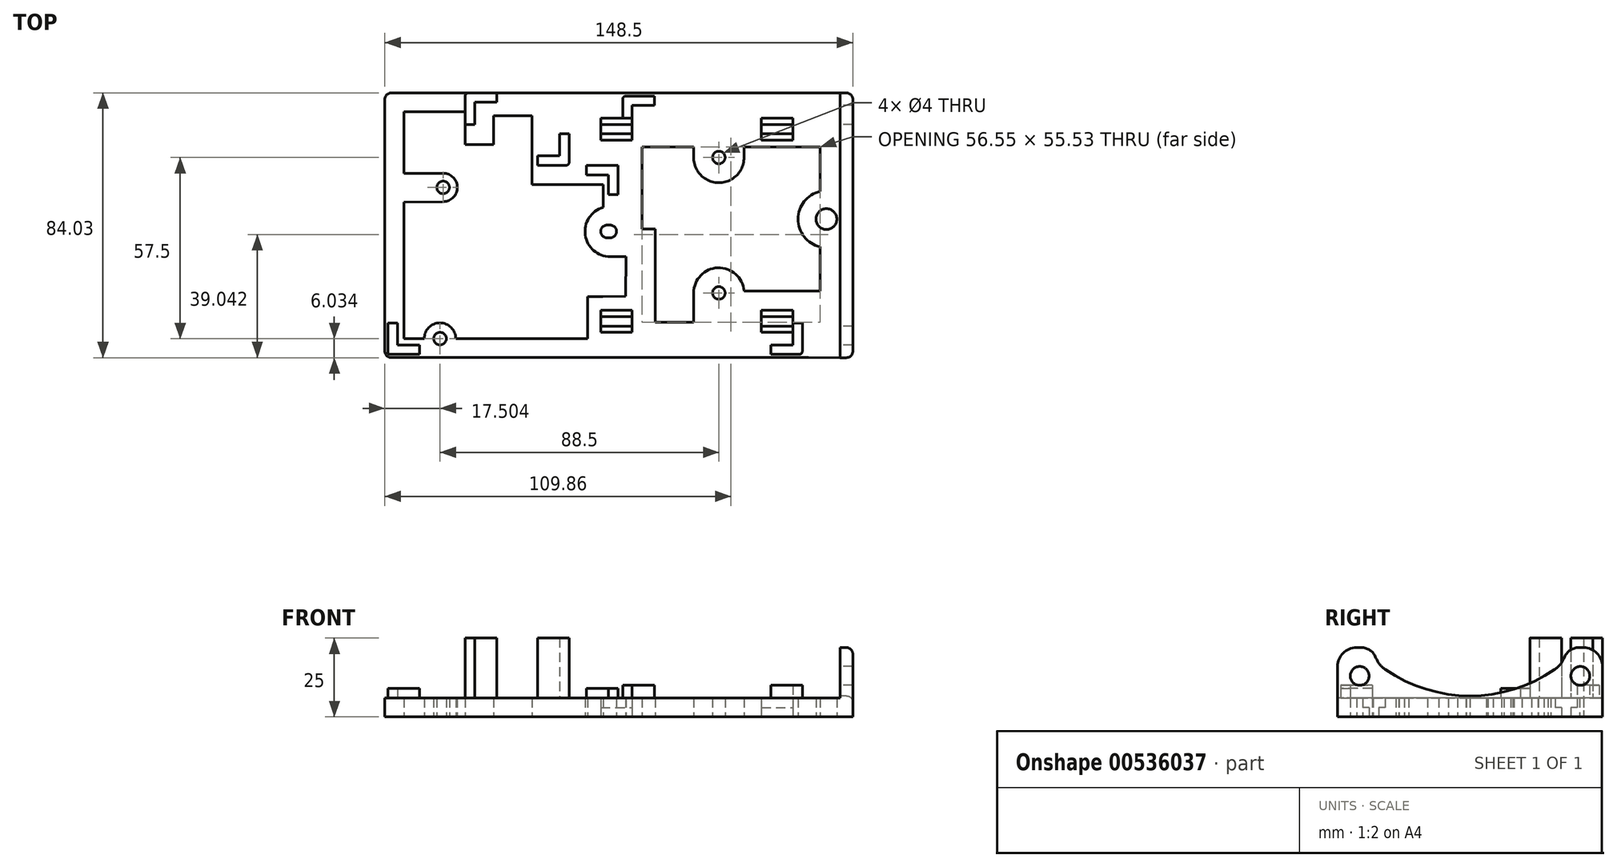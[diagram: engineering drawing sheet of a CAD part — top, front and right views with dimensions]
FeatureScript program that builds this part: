
annotation { "Feature Type Name" : "Feature", "Feature Type Description" : "" }
export const myFeature = defineFeature(function(context is Context, id is Id, definition is map)
    precondition{}
    {
        {
            var Q0;
            Q0=qCreatedBy(makeId("Top.planeOp"),FACE);
            var sketch = newSketch(context, id + "F0", { "sketchPlane" : qUnion([Q0]), "disableImprinting" : false});
            skLineSegment(sketch, "E0.bottom", {"start": v(-72.26, -23.08) * mm, "end": v(47.74, -23.08) * mm});
            skLineSegment(sketch, "E0.top", {"start": v(-72.26, 60.92) * mm, "end": v(47.74, 60.92) * mm});
            skLineSegment(sketch, "E1.bottom", {"start": v(42.74, 56.92) * mm, "end": v(-8.26, 56.92) * mm});
            skLineSegment(sketch, "E1.top", {"start": v(42.74, -19.08) * mm, "end": v(-8.26, -19.08) * mm});
            skLineSegment(sketch, "E1.right", {"start": v(-8.26, 56.92) * mm, "end": v(-8.26, -19.08) * mm});
            skLineSegment(sketch, "E2", {"start": v(-1.26, 56.92) * mm, "end": v(-1.26, 59.92) * mm});
            skLineSegment(sketch, "E3", {"start": v(-1.26, 59.92) * mm, "end": v(-11.26, 59.92) * mm});
            skLineSegment(sketch, "E4", {"start": v(-8.26, 49.92) * mm, "end": v(-8.26, 56.92) * mm});
            skLineSegment(sketch, "E5", {"start": v(35.74, -19.08) * mm, "end": v(35.74, -22.08) * mm});
            skLineSegment(sketch, "E6", {"start": v(35.74, -22.08) * mm, "end": v(45.74, -22.08) * mm});
            skLineSegment(sketch, "E7", {"start": v(45.74, -22.08) * mm, "end": v(45.74, -12.08) * mm});
            skLineSegment(sketch, "E8", {"start": v(45.74, -12.08) * mm, "end": v(42.74, -12.08) * mm});
            skLineSegment(sketch, "E9", {"start": v(42.74, -12.08) * mm, "end": v(42.74, -19.08) * mm});
            skCircle(sketch, "E10", {"center": v(19.24, 40.42) * mm, "radius": 2 * mm});
            skCircle(sketch, "E11.MirrorC", {"center": v(19.24, -2.58) * mm, "radius": 2 * mm});
            skLineSegment(sketch, "E12", {"start": v(47.74, 60.92) * mm, "end": v(57.74, 60.92) * mm});
            skLineSegment(sketch, "E13", {"start": v(57.74, 60.92) * mm, "end": v(57.74, -23.11) * mm});
            skLineSegment(sketch, "E14", {"start": v(57.74, -23.11) * mm, "end": v(47.74, -23.08) * mm});
            skLineSegment(sketch, "E15.bottom", {"start": v(-72.26, -23.08) * mm, "end": v(-86.76, -23.08) * mm});
            skLineSegment(sketch, "E15.left", {"start": v(-72.26, -23.08) * mm, "end": v(-72.26, -23.08) * mm});
            skLineSegment(sketch, "E15.right", {"start": v(-86.76, -23.08) * mm, "end": v(-86.76, -23.08) * mm});
            skLineSegment(sketch, "E16.bottom", {"start": v(-86.76, -23.08) * mm, "end": v(-72.26, -23.08) * mm});
            skLineSegment(sketch, "E16.top", {"start": v(-86.76, 60.92) * mm, "end": v(-72.26, 60.92) * mm});
            skLineSegment(sketch, "E16.left", {"start": v(-86.76, -23.08) * mm, "end": v(-86.76, 60.92) * mm});
            skLineSegment(sketch, "E17", {"start": v(-85.76, -12.08) * mm, "end": v(-85.76, -22.08) * mm});
            skLineSegment(sketch, "E18", {"start": v(-85.76, -22.08) * mm, "end": v(-75.76, -22.08) * mm});
            skLineSegment(sketch, "E19", {"start": v(-75.76, -22.08) * mm, "end": v(-75.76, -19.08) * mm});
            skLineSegment(sketch, "E20", {"start": v(-75.76, -19.08) * mm, "end": v(-82.76, -19.08) * mm});
            skLineSegment(sketch, "E21", {"start": v(-22.76, 34.92) * mm, "end": v(-22.76, 37.92) * mm});
            skLineSegment(sketch, "E22", {"start": v(-22.76, 37.92) * mm, "end": v(-12.76, 37.92) * mm});
            skLineSegment(sketch, "E23", {"start": v(-12.76, 37.92) * mm, "end": v(-12.76, 28.7) * mm});
            skLineSegment(sketch, "E24", {"start": v(-12.76, 28.7) * mm, "end": v(-15.76, 28.7) * mm});
            skLineSegment(sketch, "E25", {"start": v(-15.76, 28.7) * mm, "end": v(-15.76, 34.92) * mm});
            skCircle(sketch, "E26", {"center": v(-69.26, -17.08) * mm, "radius": 2 * mm});
            skArc(sketch, "E27", {"start": v(-15.24, 14.92) * mm, "mid": v(-13.23, 16.93) * mm, "end": v(-15.24, 18.94) * mm});
            skLineSegment(sketch, "E28", {"start": v(-22.76, 34.92) * mm, "end": v(-15.76, 34.92) * mm});
            skLineSegment(sketch, "E29", {"start": v(-82.76, -12.08) * mm, "end": v(-82.76, -19.08) * mm});
            skLineSegment(sketch, "E30", {"start": v(-51.26, 57.92) * mm, "end": v(-51.26, 60.92) * mm});
            skLineSegment(sketch, "E31", {"start": v(-51.26, 60.92) * mm, "end": v(-61.26, 60.92) * mm});
            skLineSegment(sketch, "E32", {"start": v(-61.26, 60.92) * mm, "end": v(-61.26, 50.92) * mm});
            skLineSegment(sketch, "E33", {"start": v(-61.26, 50.92) * mm, "end": v(-58.26, 50.92) * mm});
            skLineSegment(sketch, "E34", {"start": v(-38.26, 40.92) * mm, "end": v(-38.26, 37.92) * mm});
            skLineSegment(sketch, "E35", {"start": v(-38.26, 37.92) * mm, "end": v(-28.26, 37.92) * mm});
            skLineSegment(sketch, "E36", {"start": v(-28.26, 37.92) * mm, "end": v(-28.26, 47.92) * mm});
            skLineSegment(sketch, "E37", {"start": v(-28.26, 47.92) * mm, "end": v(-31.26, 47.92) * mm});
            skLineSegment(sketch, "E38", {"start": v(-31.26, 47.92) * mm, "end": v(-31.26, 40.92) * mm});
            skLineSegment(sketch, "E39", {"start": v(-38.26, 40.92) * mm, "end": v(-31.26, 40.92) * mm});
            skLineSegment(sketch, "E40", {"start": v(-58.26, 57.92) * mm, "end": v(-51.26, 57.92) * mm});
            skLineSegment(sketch, "E41", {"start": v(-58.26, 57.92) * mm, "end": v(-58.26, 50.92) * mm});
            skLineSegment(sketch, "E42.bottom", {"start": v(32.74, -8.08) * mm, "end": v(42.74, -8.08) * mm});
            skLineSegment(sketch, "E42.top", {"start": v(32.74, -15.08) * mm, "end": v(42.74, -15.08) * mm});
            skLineSegment(sketch, "E42.left", {"start": v(32.74, -8.08) * mm, "end": v(32.74, -15.08) * mm});
            skLineSegment(sketch, "E42.right", {"start": v(42.74, -8.08) * mm, "end": v(42.74, -15.08) * mm});
            skLineSegment(sketch, "E43.bottom", {"start": v(-18.26, -8.08) * mm, "end": v(-8.26, -8.08) * mm});
            skLineSegment(sketch, "E43.top", {"start": v(-18.26, -15.08) * mm, "end": v(-8.26, -15.08) * mm});
            skLineSegment(sketch, "E43.left", {"start": v(-18.26, -8.08) * mm, "end": v(-18.26, -15.08) * mm});
            skLineSegment(sketch, "E43.right", {"start": v(-8.26, -8.08) * mm, "end": v(-8.26, -15.08) * mm});
            skLineSegment(sketch, "E44", {"start": v(-18.26, -13.08) * mm, "end": v(-8.26, -13.08) * mm});
            skLineSegment(sketch, "E45", {"start": v(-18.26, -10.08) * mm, "end": v(-8.26, -10.08) * mm});
            skLineSegment(sketch, "E46", {"start": v(32.74, -10.08) * mm, "end": v(42.74, -10.08) * mm});
            skLineSegment(sketch, "E47", {"start": v(32.74, -13.08) * mm, "end": v(42.74, -13.08) * mm});
            skLineSegment(sketch, "E48.bottom", {"start": v(42.74, 52.92) * mm, "end": v(32.74, 52.92) * mm});
            skLineSegment(sketch, "E48.top", {"start": v(42.74, 45.92) * mm, "end": v(32.74, 45.92) * mm});
            skLineSegment(sketch, "E48.left", {"start": v(42.74, 52.92) * mm, "end": v(42.74, 45.92) * mm});
            skLineSegment(sketch, "E48.right", {"start": v(32.74, 52.92) * mm, "end": v(32.74, 45.92) * mm});
            skLineSegment(sketch, "E49", {"start": v(32.74, 50.92) * mm, "end": v(42.74, 50.92) * mm});
            skLineSegment(sketch, "E50", {"start": v(32.74, 47.92) * mm, "end": v(42.74, 47.92) * mm});
            skLineSegment(sketch, "E51.bottom", {"start": v(-18.26, 52.92) * mm, "end": v(-8.26, 52.92) * mm});
            skLineSegment(sketch, "E51.top", {"start": v(-18.26, 45.92) * mm, "end": v(-8.26, 45.92) * mm});
            skLineSegment(sketch, "E51.left", {"start": v(-18.26, 52.92) * mm, "end": v(-18.26, 45.92) * mm});
            skLineSegment(sketch, "E51.right", {"start": v(-8.26, 52.92) * mm, "end": v(-8.26, 45.92) * mm});
            skLineSegment(sketch, "E52", {"start": v(-18.26, 47.92) * mm, "end": v(-8.26, 47.92) * mm});
            skLineSegment(sketch, "E53", {"start": v(-11.26, 59.92) * mm, "end": v(-11.26, 52.92) * mm});
            skLineSegment(sketch, "E54", {"start": v(-11.26, 52.92) * mm, "end": v(-8.26, 52.92) * mm});
            skLineSegment(sketch, "E55", {"start": v(-18.26, 50.92) * mm, "end": v(-8.26, 50.92) * mm});
            skPoint(sketch, "E56.endSnap0", {"position": v(-15.76, 31.81) * mm});
            skLineSegment(sketch, "E57", {"start": v(-17.51, 31.81) * mm, "end": v(-40.11, 31.81) * mm});
            skLineSegment(sketch, "E58", {"start": v(-40.11, 31.81) * mm, "end": v(-40.11, 53.65) * mm});
            skLineSegment(sketch, "E59", {"start": v(-40.11, 53.65) * mm, "end": v(-52.22, 53.65) * mm});
            skLineSegment(sketch, "E60", {"start": v(-52.22, 53.65) * mm, "end": v(-52.22, 44.5) * mm});
            skLineSegment(sketch, "E61", {"start": v(-52.22, 44.5) * mm, "end": v(-61.24, 44.5) * mm});
            skLineSegment(sketch, "E62", {"start": v(-61.24, 44.5) * mm, "end": v(-61.24, 54.92) * mm});
            skLineSegment(sketch, "E63", {"start": v(-61.24, 54.92) * mm, "end": v(-80.76, 54.92) * mm});
            skLineSegment(sketch, "E64", {"start": v(-85.76, -12.08) * mm, "end": v(-82.76, -12.08) * mm});
            skLineSegment(sketch, "E65", {"start": v(-22.37, -17.08) * mm, "end": v(-22.37, -3.68) * mm});
            skLineSegment(sketch, "E66", {"start": v(-22.37, -3.68) * mm, "end": v(-17.57, -3.68) * mm});
            skLineSegment(sketch, "E67", {"start": v(-10.28, 8.95) * mm, "end": v(-10.3, -3.62) * mm});
            skLineSegment(sketch, "E68", {"start": v(-10.3, -3.62) * mm, "end": v(-17.57, -3.68) * mm});
            skLineSegment(sketch, "E69", {"start": v(-64.26, -17.08) * mm, "end": v(-22.37, -17.08) * mm});
            skLineSegment(sketch, "E70", {"start": v(-5.17, 43.7) * mm, "end": v(-5.17, 17.78) * mm});
            skLineSegment(sketch, "E71", {"start": v(-5.17, 17.78) * mm, "end": v(-0.94, 17.78) * mm});
            skLineSegment(sketch, "E72", {"start": v(-0.94, 17.78) * mm, "end": v(-0.94, -5.91) * mm});
            skLineSegment(sketch, "E73", {"start": v(-0.94, -5.91) * mm, "end": v(-0.94, -11.83) * mm});
            skLineSegment(sketch, "E74", {"start": v(-0.94, -11.83) * mm, "end": v(11.24, -11.83) * mm});
            skLineSegment(sketch, "E75", {"start": v(11.24, -11.83) * mm, "end": v(11.24, -2.58) * mm});
            skLineSegment(sketch, "E76", {"start": v(27.22, -1.96) * mm, "end": v(51.37, -1.96) * mm});
            skLineSegment(sketch, "E77", {"start": v(51.37, 43.7) * mm, "end": v(51.37, 29.64) * mm});
            skArc(sketch, "E78", {"start": v(11.24, -2.58) * mm, "mid": v(18.94, 5.42) * mm, "end": v(27.22, -1.96) * mm});
            skLineSegment(sketch, "E79", {"start": v(11.25, 40.65) * mm, "end": v(11.25, 43.7) * mm});
            skLineSegment(sketch, "E80", {"start": v(27.24, 40.53) * mm, "end": v(27.24, 43.7) * mm});
            skArc(sketch, "E81", {"start": v(27.24, 40.53) * mm, "mid": v(19.18, 32.42) * mm, "end": v(11.25, 40.65) * mm});
            skLineSegment(sketch, "E82", {"start": v(-5.17, 43.7) * mm, "end": v(11.25, 43.7) * mm});
            skLineSegment(sketch, "E83", {"start": v(27.24, 43.7) * mm, "end": v(51.37, 43.7) * mm});
            skArc(sketch, "E84", {"start": v(-15.24, 8.95) * mm, "mid": v(-23.14, 15.78) * mm, "end": v(-17.51, 24.6) * mm});
            skLineSegment(sketch, "E85", {"start": v(-17.51, 31.81) * mm, "end": v(-17.51, 24.6) * mm});
            skLineSegment(sketch, "E86", {"start": v(-80.76, 54.92) * mm, "end": v(-80.76, 39.92) * mm});
            skLineSegment(sketch, "E87", {"start": v(-80.76, 25.92) * mm, "end": v(-80.76, -17.08) * mm});
            skArc(sketch, "E88", {"start": v(-64.26, -17.08) * mm, "mid": v(-69.26, -12.08) * mm, "end": v(-74.26, -17.08) * mm});
            skLineSegment(sketch, "E89", {"start": v(-80.76, -17.08) * mm, "end": v(-74.26, -17.08) * mm});
            skCircle(sketch, "E90", {"center": v(-68.26, 30.92) * mm, "radius": 2 * mm});
            skLineSegment(sketch, "E91", {"start": v(-68.26, 35.42) * mm, "end": v(-80.76, 35.42) * mm});
            skLineSegment(sketch, "E92", {"start": v(-68.2, 26.42) * mm, "end": v(-80.76, 26.24) * mm});
            skArc(sketch, "E93", {"start": v(-68.2, 26.42) * mm, "mid": v(-63.76, 30.95) * mm, "end": v(-68.26, 35.42) * mm});
            skLineSegment(sketch, "E94", {"start": v(-80.76, 39.92) * mm, "end": v(-80.76, 35.42) * mm});
            skLineSegment(sketch, "E95", {"start": v(-80.76, 25.92) * mm, "end": v(-80.76, 26.24) * mm});
            skLineSegment(sketch, "E96.trimOffspring", {"start": v(51.37, 12.1) * mm, "end": v(51.37, -1.96) * mm});
            skCircle(sketch, "E97", {"center": v(53.37, 20.87) * mm, "radius": 3.3 * mm});
            skArc(sketch, "E98", {"start": v(51.37, 29.64) * mm, "mid": v(44.37, 20.87) * mm, "end": v(51.37, 12.1) * mm});
            skArc(sketch, "E99", {"start": v(-16.24, 18.94) * mm, "mid": v(-18.26, 16.94) * mm, "end": v(-16.26, 14.92) * mm});
            skLineSegment(sketch, "E100", {"start": v(-16.24, 18.94) * mm, "end": v(-15.24, 18.94) * mm});
            skLineSegment(sketch, "E101", {"start": v(-16.26, 14.92) * mm, "end": v(-15.24, 14.92) * mm});
            skLineSegment(sketch, "E102", {"start": v(-15.24, 8.95) * mm, "end": v(-10.28, 8.95) * mm});
            skSolve(sketch);
        }
        {
            var Q0;
            Q0=makeQuery(id+"F0.imprint","IMPRINT",FACE,{"disambiguationData":[TD([[makeQuery(id+"F0.imprint","IMPRINT",EDGE,{"derivedFrom":sQuery(id+"F0.wireOp",EDGE,"E0.bottom")}),1.0]])]});
            var Q1;
            {var subQ7=sQuery(id+"F0.wireOp",EDGE,"E1.left");Q1=makeQuery(id+"F0.imprint","IMPRINT",FACE,{"disambiguationData":[TD([[makeQuery(id+"F0.imprint","IMPRINT",EDGE,{"derivedFrom":subQ7}),-1.0]])]});}
            extrude(context, id + "F1", {"entities" : qUnion([Q0, Q1]), "depth" : 6 * mm, "offsetDistance" : 25 * mm});
        }
        {
            var Q0;
            {var subQ3=sQuery(id+"F0.wireOp",EDGE,"E2");Q0=makeQuery(id+"F0.imprint","IMPRINT",FACE,{"disambiguationData":[TD([[makeQuery(id+"F0.imprint","IMPRINT",EDGE,{"derivedFrom":subQ3}),1.0]])]});}
            var Q1;
            {var subQ0=sQuery(id+"F0.wireOp",EDGE,"E5");Q1=makeQuery(id+"F0.imprint","IMPRINT",FACE,{"disambiguationData":[TD([[makeQuery(id+"F0.imprint","IMPRINT",EDGE,{"derivedFrom":subQ0}),1.0]])]});}
            extrude(context, id + "F2", {"entities" : qUnion([Q0, Q1]), "operationType" : NewBodyOperationType.ADD, "depth" : 10 * mm, "offsetDistance" : 25 * mm});
        }
        {
            var Q0;
            Q0=makeQuery(id+"F1.opExtrude","SWEPT_FACE",FACE,{"disambiguationData":[OSD([sQuery(id+"F0.wireOp",EDGE,"E13")])]});
            var sketch = newSketch(context, id + "F3", { "sketchPlane" : qUnion([Q0])});
            skLineSegment(sketch, "E103", {"start": v(-23.11, 0) * mm, "end": v(-23.11, 22) * mm});
            skLineSegment(sketch, "E104", {"start": v(-23.11, 22) * mm, "end": v(-3.11, 22) * mm});
            skLineSegment(sketch, "E105", {"start": v(-3.11, 22) * mm, "end": v(-3.11, 6) * mm});
            skLineSegment(sketch, "E106", {"start": v(-3.11, 6) * mm, "end": v(40.92, 6) * mm});
            skLineSegment(sketch, "E107", {"start": v(40.92, 6) * mm, "end": v(40.92, 22) * mm});
            skLineSegment(sketch, "E108", {"start": v(40.92, 22) * mm, "end": v(60.92, 22) * mm});
            skLineSegment(sketch, "E109", {"start": v(60.92, 22) * mm, "end": v(60.92, 0) * mm});
            skLineSegment(sketch, "E110", {"start": v(60.92, 0) * mm, "end": v(-23.11, 0) * mm});
            skCircle(sketch, "E111", {"center": v(-3.11, 22) * mm, "radius": 8.5 * mm});
            skCircle(sketch, "E112", {"center": v(40.92, 22) * mm, "radius": 8.5 * mm});
            skCircle(sketch, "E113", {"center": v(-16.11, 13) * mm, "radius": 3 * mm});
            skCircle(sketch, "E114", {"center": v(53.92, 13) * mm, "radius": 3 * mm});
            skLineSegment(sketch, "E115", {"start": v(18.9, 57) * mm, "end": v(18.9, 13.5) * mm});
            skArc(sketch, "E116", {"start": v(45.73, 15) * mm, "mid": v(18.9, 6.67) * mm, "end": v(-7.92, 15) * mm});
            skSolve(sketch);
        }
        {
            var Q0;
            {var subQ0=sQuery(id+"F3.wireOp",EDGE,"E104");var subQ1=sQuery(id+"F3.wireOp",EDGE,"E103");var subQ2=makeQuery(id+"F3.imprint","INTERSECT",VERTEX,{"derivedFrom":[subQ1,subQ0]});Q0=makeQuery(id+"F3.imprint","IMPRINT",FACE,{"disambiguationData":[TD([[makeQuery(id+"F3.imprint","IMPRINT",EDGE,{"disambiguationData":[TD([[subQ2,1.0]])],"derivedFrom":subQ1}),-1.0]])]});}
            var Q1;
            {var subQ6=sQuery(id+"F3.wireOp",EDGE,"E106");Q1=makeQuery(id+"F3.imprint","IMPRINT",FACE,{"disambiguationData":[TD([[makeQuery(id+"F3.imprint","IMPRINT",EDGE,{"derivedFrom":subQ6}),1.0]])]});}
            var Q2;
            {var subQ0=sQuery(id+"F3.wireOp",EDGE,"E106");Q2=makeQuery(id+"F3.imprint","IMPRINT",FACE,{"disambiguationData":[TD([[makeQuery(id+"F3.imprint","IMPRINT",EDGE,{"derivedFrom":subQ0}),-1.0]])]});}
            var Q3;
            {var subQ3=sQuery(id+"F3.wireOp",EDGE,"E108");var subQ7=sQuery(id+"F3.wireOp",EDGE,"E109");var subQ9=makeQuery(id+"F3.imprint","INTERSECT",VERTEX,{"derivedFrom":[subQ3,subQ7]});Q3=makeQuery(id+"F3.imprint","IMPRINT",FACE,{"disambiguationData":[TD([[makeQuery(id+"F3.imprint","IMPRINT",EDGE,{"disambiguationData":[TD([[subQ9,1.0]])],"derivedFrom":subQ3}),-1.0]])]});}
            extrude(context, id + "F4", {"entities" : qUnion([Q0, Q1, Q2, Q3]), "operationType" : NewBodyOperationType.ADD, "depth" : 4 * mm, "offsetDistance" : 25 * mm});
        }
        {
            var Q0;
            Q0=makeQuery(id+"F4.opExtrude","SWEPT_EDGE",EDGE,{"disambiguationData":[OSD([sQuery(id+"F3.wireOp",EDGE,"E104"),sQuery(id+"F3.wireOp",EDGE,"E111")])]});
            fillet(context, id + "F5", {"entities" : qUnion([Q0]), "radius" : 5 * mm, "tangentPropagation" : true, "allowEdgeOverflow" : false});
        }
        {
            var Q0;
            Q0=makeQuery(id+"F4.opExtrude","SWEPT_EDGE",EDGE,{"disambiguationData":[OSD([sQuery(id+"F3.wireOp",EDGE,"E108"),sQuery(id+"F3.wireOp",EDGE,"E112")])]});
            fillet(context, id + "F6", {"entities" : qUnion([Q0]), "radius" : 5 * mm, "tangentPropagation" : true, "allowEdgeOverflow" : false});
        }
        {
            var Q0;
            Q0=makeQuery(id+"F4.opExtrude","SWEPT_EDGE",EDGE,{"disambiguationData":[OSD([sQuery(id+"F3.wireOp",EDGE,"E108"),sQuery(id+"F3.wireOp",EDGE,"E109")])]});
            fillet(context, id + "F7", {"entities" : qUnion([Q0]), "radius" : 6 * mm, "tangentPropagation" : true, "allowEdgeOverflow" : false});
        }
        {
            var Q0;
            Q0=makeQuery(id+"F4.opExtrude","SWEPT_EDGE",EDGE,{"disambiguationData":[OSD([sQuery(id+"F3.wireOp",EDGE,"E103"),sQuery(id+"F3.wireOp",EDGE,"E104")])]});
            fillet(context, id + "F8", {"entities" : qUnion([Q0]), "radius" : 6 * mm, "tangentPropagation" : true, "allowEdgeOverflow" : false});
        }
        {
            var Q0;
            {var subQ4=sQuery(id+"F0.wireOp",EDGE,"E30");Q0=makeQuery(id+"F0.imprint","IMPRINT",FACE,{"disambiguationData":[TD([[makeQuery(id+"F0.imprint","IMPRINT",EDGE,{"derivedFrom":subQ4}),1.0]])]});}
            var Q1;
            Q1=makeQuery(id+"F0.imprint","IMPRINT",FACE,{"disambiguationData":[TD([[makeQuery(id+"F0.imprint","IMPRINT",EDGE,{"derivedFrom":sQuery(id+"F0.wireOp",EDGE,"E34")}),1.0]])]});
            extrude(context, id + "F9", {"entities" : qUnion([Q0, Q1]), "operationType" : NewBodyOperationType.ADD, "depth" : 25 * mm, "offsetDistance" : 25 * mm});
        }
        {
            var Q0;
            {var subQ3=sQuery(id+"F0.wireOp",EDGE,"E55");Q0=makeQuery(id+"F0.imprint","IMPRINT",FACE,{"disambiguationData":[TD([[makeQuery(id+"F0.imprint","IMPRINT",EDGE,{"derivedFrom":subQ3}),1.0]])]});}
            var Q1;
            {var subQ0=sQuery(id+"F0.wireOp",EDGE,"E51.top");Q1=makeQuery(id+"F0.imprint","IMPRINT",FACE,{"disambiguationData":[TD([[makeQuery(id+"F0.imprint","IMPRINT",EDGE,{"derivedFrom":subQ0}),1.0]])]});}
            var Q2;
            {var subQ0=sQuery(id+"F0.wireOp",EDGE,"E48.bottom");Q2=makeQuery(id+"F0.imprint","IMPRINT",FACE,{"disambiguationData":[TD([[makeQuery(id+"F0.imprint","IMPRINT",EDGE,{"derivedFrom":subQ0}),1.0]])]});}
            var Q3;
            {var subQ0=sQuery(id+"F0.wireOp",EDGE,"E48.top");Q3=makeQuery(id+"F0.imprint","IMPRINT",FACE,{"disambiguationData":[TD([[makeQuery(id+"F0.imprint","IMPRINT",EDGE,{"derivedFrom":subQ0}),-1.0]])]});}
            var Q4;
            {var subQ0=sQuery(id+"F0.wireOp",EDGE,"E42.bottom");Q4=makeQuery(id+"F0.imprint","IMPRINT",FACE,{"disambiguationData":[TD([[makeQuery(id+"F0.imprint","IMPRINT",EDGE,{"derivedFrom":subQ0}),-1.0]])]});}
            var Q5;
            {var subQ0=sQuery(id+"F0.wireOp",EDGE,"E42.top");Q5=makeQuery(id+"F0.imprint","IMPRINT",FACE,{"disambiguationData":[TD([[makeQuery(id+"F0.imprint","IMPRINT",EDGE,{"derivedFrom":subQ0}),1.0]])]});}
            var Q6;
            {var subQ0=sQuery(id+"F0.wireOp",EDGE,"E43.top");Q6=makeQuery(id+"F0.imprint","IMPRINT",FACE,{"disambiguationData":[TD([[makeQuery(id+"F0.imprint","IMPRINT",EDGE,{"derivedFrom":subQ0}),1.0]])]});}
            var Q7;
            {var subQ0=sQuery(id+"F0.wireOp",EDGE,"E43.bottom");Q7=makeQuery(id+"F0.imprint","IMPRINT",FACE,{"disambiguationData":[TD([[makeQuery(id+"F0.imprint","IMPRINT",EDGE,{"derivedFrom":subQ0}),-1.0]])]});}
            extrude(context, id + "F10", {"entities" : qUnion([Q0, Q1, Q2, Q3, Q4, Q5, Q6, Q7]), "operationType" : NewBodyOperationType.ADD, "depth" : 3 * mm, "offsetDistance" : 25 * mm});
        }
        {
            var Q0;
            Q0=makeQuery(id+"Ffwyr1q8zjNAo8w_0.opExtrude","SWEPT_EDGE",EDGE,{"disambiguationData":[OSD([sQuery(id+"F0.wireOp",EDGE,"E17"),sQuery(id+"F0.wireOp",EDGE,"E18")])]});
            var Q1;
            Q1=makeQuery(id+"F1.opExtrude","SWEPT_EDGE",EDGE,{"disambiguationData":[OSD([sQuery(id+"F0.wireOp",EDGE,"E15.bottom"),sQuery(id+"F0.wireOp",EDGE,"E16.left")])]});
            fillet(context, id + "F11", {"entities" : qUnion([Q0, Q1]), "radius" : 2 * mm, "tangentPropagation" : true, "allowEdgeOverflow" : false});
        }
        {
            var Q0;
            Q0=makeQuery(id+"F2.opExtrude","SWEPT_EDGE",EDGE,{"disambiguationData":[OSD([sQuery(id+"F0.wireOp",EDGE,"E3"),sQuery(id+"F0.wireOp",EDGE,"E53")])]});
            var Q1;
            Q1=makeQuery(id+"F9.opExtrude","SWEPT_EDGE",EDGE,{"disambiguationData":[OSD([sQuery(id+"F0.wireOp",EDGE,"E0.top"),sQuery(id+"F0.wireOp",EDGE,"E32")])]});
            var Q2;
            Q2=makeQuery(id+"F2.opExtrude","SWEPT_EDGE",EDGE,{"disambiguationData":[OSD([sQuery(id+"F0.wireOp",EDGE,"E6"),sQuery(id+"F0.wireOp",EDGE,"E7")])]});
            var Q3;
            Q3=makeQuery(id+"F9.opExtrude","SWEPT_EDGE",EDGE,{"disambiguationData":[OSD([sQuery(id+"F0.wireOp",EDGE,"E35"),sQuery(id+"F0.wireOp",EDGE,"E36")])]});
            var Q4;
            Q4=makeQuery(id+"FGamisbfVxoSGgb_0.opExtrude","SWEPT_EDGE",EDGE,{"disambiguationData":[OSD([sQuery(id+"F0.wireOp",EDGE,"E22"),sQuery(id+"F0.wireOp",EDGE,"E23")])]});
            fillet(context, id + "F12", {"entities" : qUnion([Q0, Q1, Q2, Q3, Q4]), "radius" : 1 * mm, "tangentPropagation" : true, "allowEdgeOverflow" : false});
        }
        {
            var Q0;
            Q0=makeQuery(id+"F4.opExtrude","CAP_EDGE",EDGE,{"disambiguationData":[OSD([sQuery(id+"F3.wireOp",EDGE,"E116")])],"isStart":false});
            var Q1;
            Q1=makeQuery(id+"F4.opExtrude","CAP_EDGE",EDGE,{"disambiguationData":[OSD([sQuery(id+"F3.wireOp",EDGE,"E112")])],"isStart":false});
            var Q2;
            {var subQ0=sQuery(id+"F3.wireOp",EDGE,"E109");var subQ1=sQuery(id+"F3.wireOp",EDGE,"E108");Q2=makeQuery(id+"F7.opFillet","BLEND_EDGE",EDGE,{"blendedFrom":[makeQuery(id+"F4.opExtrude","SWEPT_EDGE",EDGE,{"disambiguationData":[OSD([subQ1,subQ0])]}),makeQuery(id+"F4.opExtrude","CAP_FACE",FACE,{"disambiguationData":[OSD([sQuery(id+"F3.wireOp",EDGE,"E103"),sQuery(id+"F3.wireOp",EDGE,"E104"),subQ1,subQ0,sQuery(id+"F3.wireOp",EDGE,"E110"),sQuery(id+"F3.wireOp",EDGE,"E111"),sQuery(id+"F3.wireOp",EDGE,"E112"),sQuery(id+"F3.wireOp",EDGE,"E113"),sQuery(id+"F3.wireOp",EDGE,"E114"),sQuery(id+"F3.wireOp",EDGE,"E116")])],"isStart":false})],"blendedInto":[makeQuery(id+"F4.opExtrude","CAP_FACE",FACE,{"disambiguationData":[OSD([sQuery(id+"F3.wireOp",EDGE,"E103"),sQuery(id+"F3.wireOp",EDGE,"E104"),subQ1,subQ0,sQuery(id+"F3.wireOp",EDGE,"E110"),sQuery(id+"F3.wireOp",EDGE,"E111"),sQuery(id+"F3.wireOp",EDGE,"E112"),sQuery(id+"F3.wireOp",EDGE,"E113"),sQuery(id+"F3.wireOp",EDGE,"E114"),sQuery(id+"F3.wireOp",EDGE,"E116")])],"isStart":false})]});}
            var Q3;
            Q3=makeQuery(id+"F4.opExtrude","CAP_EDGE",EDGE,{"disambiguationData":[OSD([sQuery(id+"F3.wireOp",EDGE,"E108")])],"isStart":false});
            var Q4;
            {var subQ0=sQuery(id+"F3.wireOp",EDGE,"E112");var subQ1=sQuery(id+"F3.wireOp",EDGE,"E108");Q4=makeQuery(id+"F6.opFillet","BLEND_EDGE",EDGE,{"blendedFrom":[makeQuery(id+"F4.opExtrude","SWEPT_EDGE",EDGE,{"disambiguationData":[OSD([subQ1,subQ0])]}),makeQuery(id+"F4.opExtrude","CAP_FACE",FACE,{"disambiguationData":[OSD([sQuery(id+"F3.wireOp",EDGE,"E103"),sQuery(id+"F3.wireOp",EDGE,"E104"),subQ1,sQuery(id+"F3.wireOp",EDGE,"E109"),sQuery(id+"F3.wireOp",EDGE,"E110"),sQuery(id+"F3.wireOp",EDGE,"E111"),subQ0,sQuery(id+"F3.wireOp",EDGE,"E113"),sQuery(id+"F3.wireOp",EDGE,"E114"),sQuery(id+"F3.wireOp",EDGE,"E116")])],"isStart":false})],"blendedInto":[makeQuery(id+"F4.opExtrude","CAP_FACE",FACE,{"disambiguationData":[OSD([sQuery(id+"F3.wireOp",EDGE,"E103"),sQuery(id+"F3.wireOp",EDGE,"E104"),subQ1,sQuery(id+"F3.wireOp",EDGE,"E109"),sQuery(id+"F3.wireOp",EDGE,"E110"),sQuery(id+"F3.wireOp",EDGE,"E111"),subQ0,sQuery(id+"F3.wireOp",EDGE,"E113"),sQuery(id+"F3.wireOp",EDGE,"E114"),sQuery(id+"F3.wireOp",EDGE,"E116")])],"isStart":false})]});}
            var Q5;
            Q5=makeQuery(id+"F4.opExtrude","CAP_EDGE",EDGE,{"disambiguationData":[OSD([sQuery(id+"F3.wireOp",EDGE,"E109")])],"isStart":false});
            var Q6;
            Q6=makeQuery(id+"F4.opExtrude","CAP_EDGE",EDGE,{"disambiguationData":[OSD([sQuery(id+"F3.wireOp",EDGE,"E111")])],"isStart":false});
            var Q7;
            {var subQ0=sQuery(id+"F3.wireOp",EDGE,"E111");var subQ1=sQuery(id+"F3.wireOp",EDGE,"E104");Q7=makeQuery(id+"F5.opFillet","BLEND_EDGE",EDGE,{"blendedFrom":[makeQuery(id+"F4.opExtrude","SWEPT_EDGE",EDGE,{"disambiguationData":[OSD([subQ1,subQ0])]}),makeQuery(id+"F4.opExtrude","CAP_FACE",FACE,{"disambiguationData":[OSD([sQuery(id+"F3.wireOp",EDGE,"E103"),subQ1,sQuery(id+"F3.wireOp",EDGE,"E108"),sQuery(id+"F3.wireOp",EDGE,"E109"),sQuery(id+"F3.wireOp",EDGE,"E110"),subQ0,sQuery(id+"F3.wireOp",EDGE,"E112"),sQuery(id+"F3.wireOp",EDGE,"E113"),sQuery(id+"F3.wireOp",EDGE,"E114"),sQuery(id+"F3.wireOp",EDGE,"E116")])],"isStart":false})],"blendedInto":[makeQuery(id+"F4.opExtrude","CAP_FACE",FACE,{"disambiguationData":[OSD([sQuery(id+"F3.wireOp",EDGE,"E103"),subQ1,sQuery(id+"F3.wireOp",EDGE,"E108"),sQuery(id+"F3.wireOp",EDGE,"E109"),sQuery(id+"F3.wireOp",EDGE,"E110"),subQ0,sQuery(id+"F3.wireOp",EDGE,"E112"),sQuery(id+"F3.wireOp",EDGE,"E113"),sQuery(id+"F3.wireOp",EDGE,"E114"),sQuery(id+"F3.wireOp",EDGE,"E116")])],"isStart":false})]});}
            var Q8;
            Q8=makeQuery(id+"F4.opExtrude","CAP_EDGE",EDGE,{"disambiguationData":[OSD([sQuery(id+"F3.wireOp",EDGE,"E104")])],"isStart":false});
            var Q9;
            {var subQ0=sQuery(id+"F3.wireOp",EDGE,"E104");var subQ1=sQuery(id+"F3.wireOp",EDGE,"E103");Q9=makeQuery(id+"F8.opFillet","BLEND_EDGE",EDGE,{"blendedFrom":[makeQuery(id+"F4.opExtrude","SWEPT_EDGE",EDGE,{"disambiguationData":[OSD([subQ1,subQ0])]}),makeQuery(id+"F4.opExtrude","CAP_FACE",FACE,{"disambiguationData":[OSD([subQ1,subQ0,sQuery(id+"F3.wireOp",EDGE,"E108"),sQuery(id+"F3.wireOp",EDGE,"E109"),sQuery(id+"F3.wireOp",EDGE,"E110"),sQuery(id+"F3.wireOp",EDGE,"E111"),sQuery(id+"F3.wireOp",EDGE,"E112"),sQuery(id+"F3.wireOp",EDGE,"E113"),sQuery(id+"F3.wireOp",EDGE,"E114"),sQuery(id+"F3.wireOp",EDGE,"E116")])],"isStart":false})],"blendedInto":[makeQuery(id+"F4.opExtrude","CAP_FACE",FACE,{"disambiguationData":[OSD([subQ1,subQ0,sQuery(id+"F3.wireOp",EDGE,"E108"),sQuery(id+"F3.wireOp",EDGE,"E109"),sQuery(id+"F3.wireOp",EDGE,"E110"),sQuery(id+"F3.wireOp",EDGE,"E111"),sQuery(id+"F3.wireOp",EDGE,"E112"),sQuery(id+"F3.wireOp",EDGE,"E113"),sQuery(id+"F3.wireOp",EDGE,"E114"),sQuery(id+"F3.wireOp",EDGE,"E116")])],"isStart":false})]});}
            var Q10;
            Q10=makeQuery(id+"F4.opExtrude","CAP_EDGE",EDGE,{"disambiguationData":[OSD([sQuery(id+"F3.wireOp",EDGE,"E103")])],"isStart":false});
            fillet(context, id + "F13", {"entities" : qUnion([Q0, Q1, Q2, Q3, Q4, Q5, Q6, Q7, Q8, Q9, Q10]), "radius" : 2 * mm, "tangentPropagation" : true, "allowEdgeOverflow" : false});
        }
        {
            var Q0;
            Q0=makeQuery(id+"F0.imprint","IMPRINT",FACE,{"disambiguationData":[TD([[makeQuery(id+"F0.imprint","IMPRINT",EDGE,{"derivedFrom":sQuery(id+"F0.wireOp",EDGE,"E17")}),1.0]])]});
            var Q1;
            Q1=makeQuery(id+"F0.imprint","IMPRINT",FACE,{"disambiguationData":[TD([[makeQuery(id+"F0.imprint","IMPRINT",EDGE,{"derivedFrom":sQuery(id+"F0.wireOp",EDGE,"E21")}),-1.0]])]});
            extrude(context, id + "F14", {"entities" : qUnion([Q0, Q1]), "operationType" : NewBodyOperationType.ADD, "depth" : 9 * mm, "offsetDistance" : 25 * mm});
        }
        {
            var Q0;
            Q0=makeQuery(id+"F1.opExtrude","SWEPT_EDGE",EDGE,{"disambiguationData":[OSD([sQuery(id+"F0.wireOp",EDGE,"E16.top"),sQuery(id+"F0.wireOp",EDGE,"E16.left")])]});
            fillet(context, id + "F15", {"entities" : qUnion([Q0]), "radius" : 2 * mm, "tangentPropagation" : true, "allowEdgeOverflow" : false});
        }
    });
